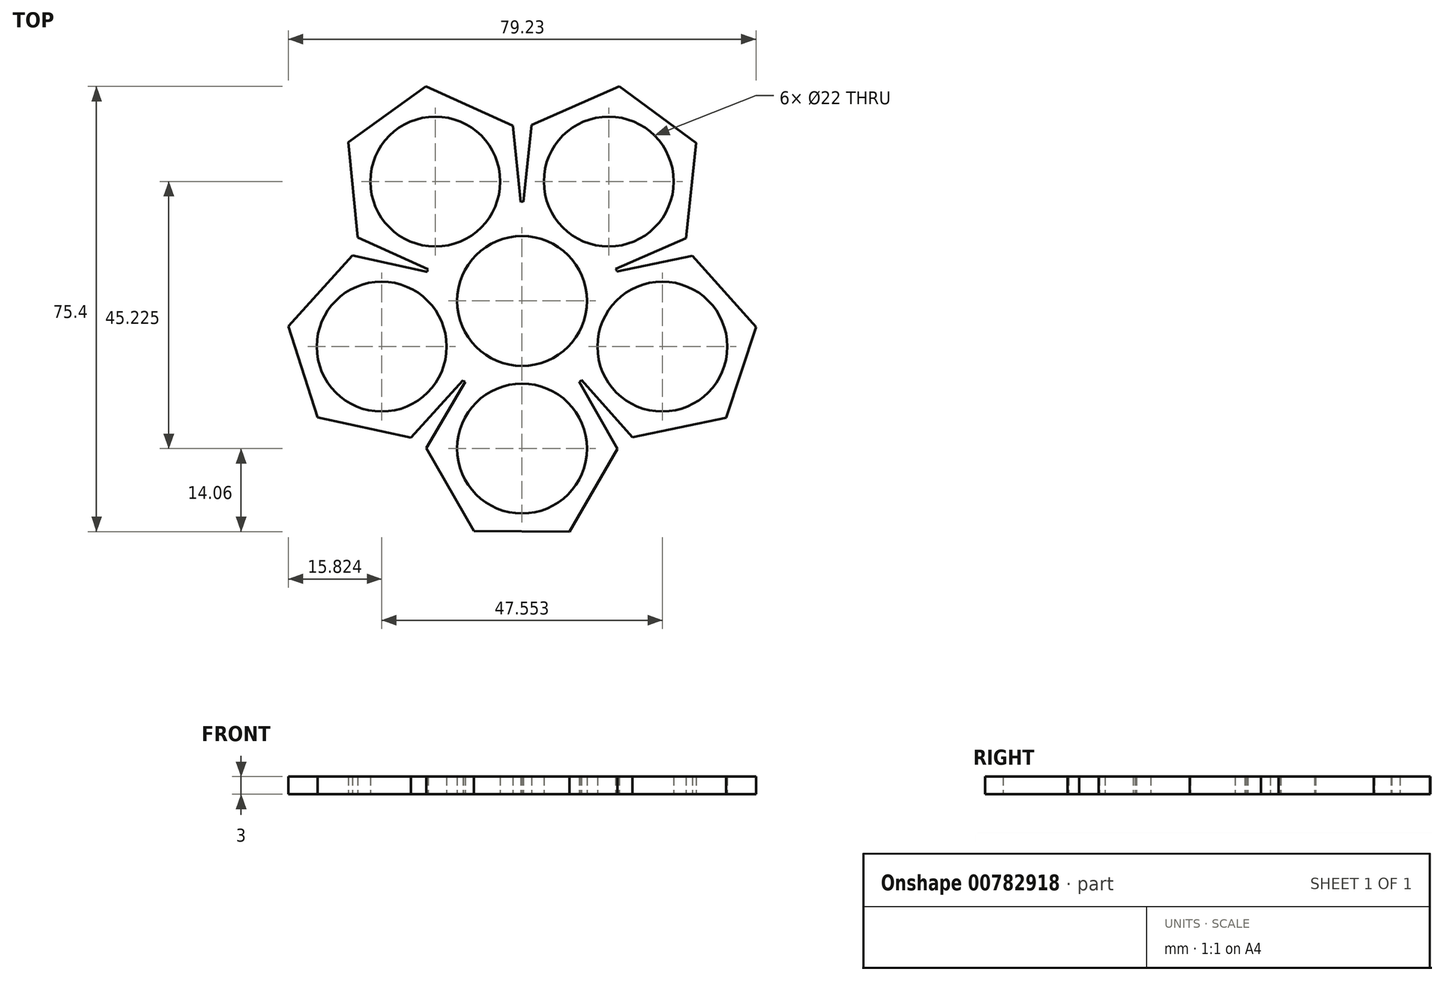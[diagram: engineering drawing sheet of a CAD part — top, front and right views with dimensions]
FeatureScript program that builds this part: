
annotation { "Feature Type Name" : "Feature", "Feature Type Description" : "" }
export const myFeature = defineFeature(function(context is Context, id is Id, definition is map)
    precondition{}
    {
        {
            var Q0;
            Q0=qCreatedBy(makeId("Top.planeOp"),FACE);
            var sketch = newSketch(context, id + "F0", { "sketchPlane" : qUnion([Q0])});
            skArc(sketch, "E0", {"start": v(-6.47, -8.9) * mm, "mid": v(0, -11) * mm, "end": v(6.47, -8.9) * mm});
            skLineSegment(sketch, "E1.0", {"start": v(9.95, -13.7) * mm, "end": v(9.7, -13.7) * mm});
            skPoint(sketch, "E1.0.midPoint", {"position": v(0, -13.7) * mm});
            skCircle(sketch, "E2", {"center": v(0, -25) * mm, "radius": 11 * mm});
            skLineSegment(sketch, "E3.0", {"start": v(-8.16, -38.99) * mm, "end": v(-16.2, -24.93) * mm});
            skLineSegment(sketch, "E3.1", {"start": v(-16.2, -24.93) * mm, "end": v(-9.64, -13.7) * mm});
            skLineSegment(sketch, "E3.2", {"start": v(-0.8, -10.97) * mm, "end": v(0.7, -10.98) * mm});
            skLineSegment(sketch, "E3.3", {"start": v(9.7, -13.7) * mm, "end": v(16.2, -25.07) * mm});
            skLineSegment(sketch, "E3.4", {"start": v(16.2, -25.07) * mm, "end": v(8.03, -39.06) * mm});
            skLineSegment(sketch, "E3.5", {"start": v(8.03, -39.06) * mm, "end": v(-8.16, -38.99) * mm});
            skPoint(sketch, "E3.0.midPoint", {"position": v(-12.18, -31.96) * mm});
            skLineSegment(sketch, "E4.trimOffspring", {"start": v(-9.64, -13.7) * mm, "end": v(-9.95, -13.7) * mm});
            skPoint(sketch, "E5.1.0", {"position": v(13.02, -4.23) * mm});
            skPoint(sketch, "E5.1.1", {"position": v(26.63, -21.46) * mm});
            skLineSegment(sketch, "E5.1.3", {"start": v(39.63, -4.43) * mm, "end": v(34.56, -19.8) * mm});
            skLineSegment(sketch, "E5.1.4", {"start": v(28.85, 7.65) * mm, "end": v(39.63, -4.43) * mm});
            skLineSegment(sketch, "E5.1.5", {"start": v(16.02, 4.99) * mm, "end": v(28.85, 7.65) * mm});
            skLineSegment(sketch, "E5.1.6", {"start": v(18.7, -23.1) * mm, "end": v(10.04, -13.4) * mm});
            skCircle(sketch, "E5.1.7", {"center": v(23.78, -7.73) * mm, "radius": 11 * mm});
            skLineSegment(sketch, "E5.1.9", {"start": v(34.56, -19.8) * mm, "end": v(18.7, -23.1) * mm});
            skArc(sketch, "E5.1.10", {"start": v(6.47, -8.9) * mm, "mid": v(10.46, -3.4) * mm, "end": v(10.46, 3.4) * mm});
            skLineSegment(sketch, "E5.1.11", {"start": v(10.19, -4.16) * mm, "end": v(10.66, -2.72) * mm});
            skLineSegment(sketch, "E5.1.12", {"start": v(16.1, 5.23) * mm, "end": v(16.02, 4.99) * mm});
            skLineSegment(sketch, "E5.1.13", {"start": v(10.04, -13.4) * mm, "end": v(9.95, -13.7) * mm});
            skPoint(sketch, "E5.2.0", {"position": v(8.05, 11.08) * mm});
            skPoint(sketch, "E5.2.1", {"position": v(28.64, 18.7) * mm});
            skLineSegment(sketch, "E5.2.3", {"start": v(16.46, 36.32) * mm, "end": v(29.52, 26.75) * mm});
            skLineSegment(sketch, "E5.2.4", {"start": v(1.63, 29.8) * mm, "end": v(16.46, 36.32) * mm});
            skLineSegment(sketch, "E5.2.5", {"start": v(0.2, 16.77) * mm, "end": v(1.63, 29.8) * mm});
            skLineSegment(sketch, "E5.2.6", {"start": v(27.75, 10.65) * mm, "end": v(15.85, 5.41) * mm});
            skCircle(sketch, "E5.2.7", {"center": v(14.7, 20.23) * mm, "radius": 11 * mm});
            skLineSegment(sketch, "E5.2.9", {"start": v(29.52, 26.75) * mm, "end": v(27.75, 10.65) * mm});
            skArc(sketch, "E5.2.10", {"start": v(10.46, 3.4) * mm, "mid": v(6.47, 8.9) * mm, "end": v(0, 11) * mm});
            skLineSegment(sketch, "E5.2.11", {"start": v(7.1, 8.4) * mm, "end": v(5.88, 9.3) * mm});
            skLineSegment(sketch, "E5.2.12", {"start": v(0, 16.92) * mm, "end": v(0.2, 16.77) * mm});
            skLineSegment(sketch, "E5.2.13", {"start": v(15.85, 5.41) * mm, "end": v(16.1, 5.23) * mm});
            skPoint(sketch, "E5.3.0", {"position": v(-8.05, 11.08) * mm});
            skPoint(sketch, "E5.3.1", {"position": v(-8.93, 33.01) * mm});
            skLineSegment(sketch, "E5.3.3", {"start": v(-29.46, 26.88) * mm, "end": v(-16.32, 36.34) * mm});
            skLineSegment(sketch, "E5.3.4", {"start": v(-27.84, 10.76) * mm, "end": v(-29.46, 26.88) * mm});
            skLineSegment(sketch, "E5.3.5", {"start": v(-15.89, 5.38) * mm, "end": v(-27.84, 10.76) * mm});
            skLineSegment(sketch, "E5.3.6", {"start": v(-1.55, 29.69) * mm, "end": v(-0.25, 16.74) * mm});
            skCircle(sketch, "E5.3.7", {"center": v(-14.7, 20.23) * mm, "radius": 11 * mm});
            skLineSegment(sketch, "E5.3.9", {"start": v(-16.32, 36.34) * mm, "end": v(-1.55, 29.69) * mm});
            skArc(sketch, "E5.3.10", {"start": v(0, 11) * mm, "mid": v(-6.47, 8.9) * mm, "end": v(-10.46, 3.4) * mm});
            skLineSegment(sketch, "E5.3.11", {"start": v(-5.8, 9.35) * mm, "end": v(-7.02, 8.47) * mm});
            skLineSegment(sketch, "E5.3.12", {"start": v(-16.1, 5.23) * mm, "end": v(-15.89, 5.38) * mm});
            skLineSegment(sketch, "E5.3.13", {"start": v(-0.25, 16.74) * mm, "end": v(0, 16.92) * mm});
            skPoint(sketch, "E5.4.0", {"position": v(-13.02, -4.23) * mm});
            skPoint(sketch, "E5.4.1", {"position": v(-34.16, 1.7) * mm});
            skLineSegment(sketch, "E5.4.3", {"start": v(-34.67, -19.71) * mm, "end": v(-39.6, -4.29) * mm});
            skLineSegment(sketch, "E5.4.4", {"start": v(-18.84, -23.15) * mm, "end": v(-34.67, -19.71) * mm});
            skLineSegment(sketch, "E5.4.5", {"start": v(-10.03, -13.45) * mm, "end": v(-18.84, -23.15) * mm});
            skLineSegment(sketch, "E5.4.6", {"start": v(-28.71, 7.7) * mm, "end": v(-16, 4.94) * mm});
            skCircle(sketch, "E5.4.7", {"center": v(-23.78, -7.73) * mm, "radius": 11 * mm});
            skLineSegment(sketch, "E5.4.9", {"start": v(-39.6, -4.29) * mm, "end": v(-28.71, 7.7) * mm});
            skArc(sketch, "E5.4.10", {"start": v(-10.46, 3.4) * mm, "mid": v(-10.46, -3.4) * mm, "end": v(-6.47, -8.9) * mm});
            skLineSegment(sketch, "E5.4.11", {"start": v(-10.68, -2.63) * mm, "end": v(-10.22, -4.06) * mm});
            skLineSegment(sketch, "E5.4.12", {"start": v(-9.95, -13.7) * mm, "end": v(-10.03, -13.45) * mm});
            skLineSegment(sketch, "E5.4.13", {"start": v(-16, 4.94) * mm, "end": v(-16.1, 5.23) * mm});
            skSolve(sketch);
        }
        {
            var Q0;
            Q0 = qSketchRegion(id + "F0", true);
            extrude(context, id + "F1", {"entities" : qUnion([Q0]), "depth" : 3 * mm, "offsetDistance" : 25 * mm});
        }
    });
